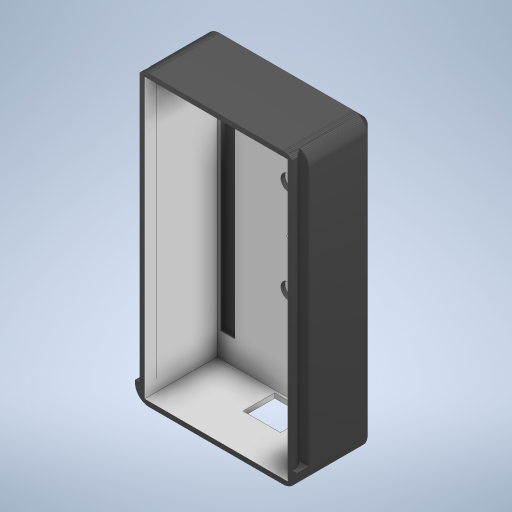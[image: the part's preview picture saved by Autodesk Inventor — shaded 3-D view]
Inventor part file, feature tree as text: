
AUTODESK INVENTOR PART (.ipt)
format: ipt  version: 2024.3 (Build 283343000, 343)  size: 1,387,008 bytes
history: native  units: mm
features: other x4, extrude x3, sketch x3
ambient origin geometry x8: Origin, YZ Plane, XZ Plane, XY Plane, X Axis, Y Axis, Z Axis, Center Point
bodies: Body1 (feature_tree)
feature tree (10):
  other  "ESP32_DEVKIT_V1_Carcasa.ipt"
  extrude  "Extrusión1"  Depth=20.0mm
  extrude  "Extrusión4"  Depth=29.0mm
  extrude  "Extrusión5"  Depth=20.0mm TaperAngle=0.0deg
  other  "Sólido1::ESP32_DEVKIT_V1_Carcasa.ipt"
  other  "OperaciónIdentificador1"
  sketch  "Boceto1"  dims[d0=20.0mm d1=1.85mm]
  sketch  "Boceto4"  dims[d2=49.0mm d3=29.0mm]
  sketch  "Boceto5"  dims[d4=10.0mm d5=0.0mm d19=20.0mm d20=0.0mm d21=2.0mm d22=2.0mm d23=2.0mm d24=2.0mm d25=31.0mm d26=0.0mm d28=15.9mm d29=13.5mm]
  other  "Sólido1"
